# Revit family: Basin-Semi-Recessed-Caroma Teo 460
name_source: partatom
category: Plumbing Fixtures
revit_build: Autodesk Revit MEP 2014 (Build: 20140709_2115(x64)
units: mm (PartAtom-declared; Revit-internal decimal feet)

## types (1)
- This family uses a type catalogue
    1TapHoles = Yes
    Assembly Code = D2010310
    Default Elevation = 1219 mm
    Depth = 140 mm  [stored 0.459318 ft]
    Length = 466 mm  [stored 1.52887 ft]
    Manufacturer = GWA Bathrooms & Kitchens
    Material_ANZRS = Porcelain-White-Caroma
    ModifiedIssue_ANZRS = 20151013.54 $
    TapHole1 = 82 mm  [stored 0.269029 ft]
    Type Comments = Caroma Teo 460 Semi Recessed Basin
    URL = http://www.specify.caroma.com.au
    WFU = 1
    Waste = Metal-Chrome-Caroma
    WasteDiameter = 30 mm  [stored 0.0984252 ft]
    WasteOutlet_ANZRS = 0
    Width = 460 mm  [stored 1.50919 ft]

note: [stored X ft] marks values corroborated as IEEE doubles in the binary element streams (Revit-internal decimal feet)

## geometry (parser evidence)
native form markers: Blend x8, Sweep x1
no freeform markers — native parametric forms only
